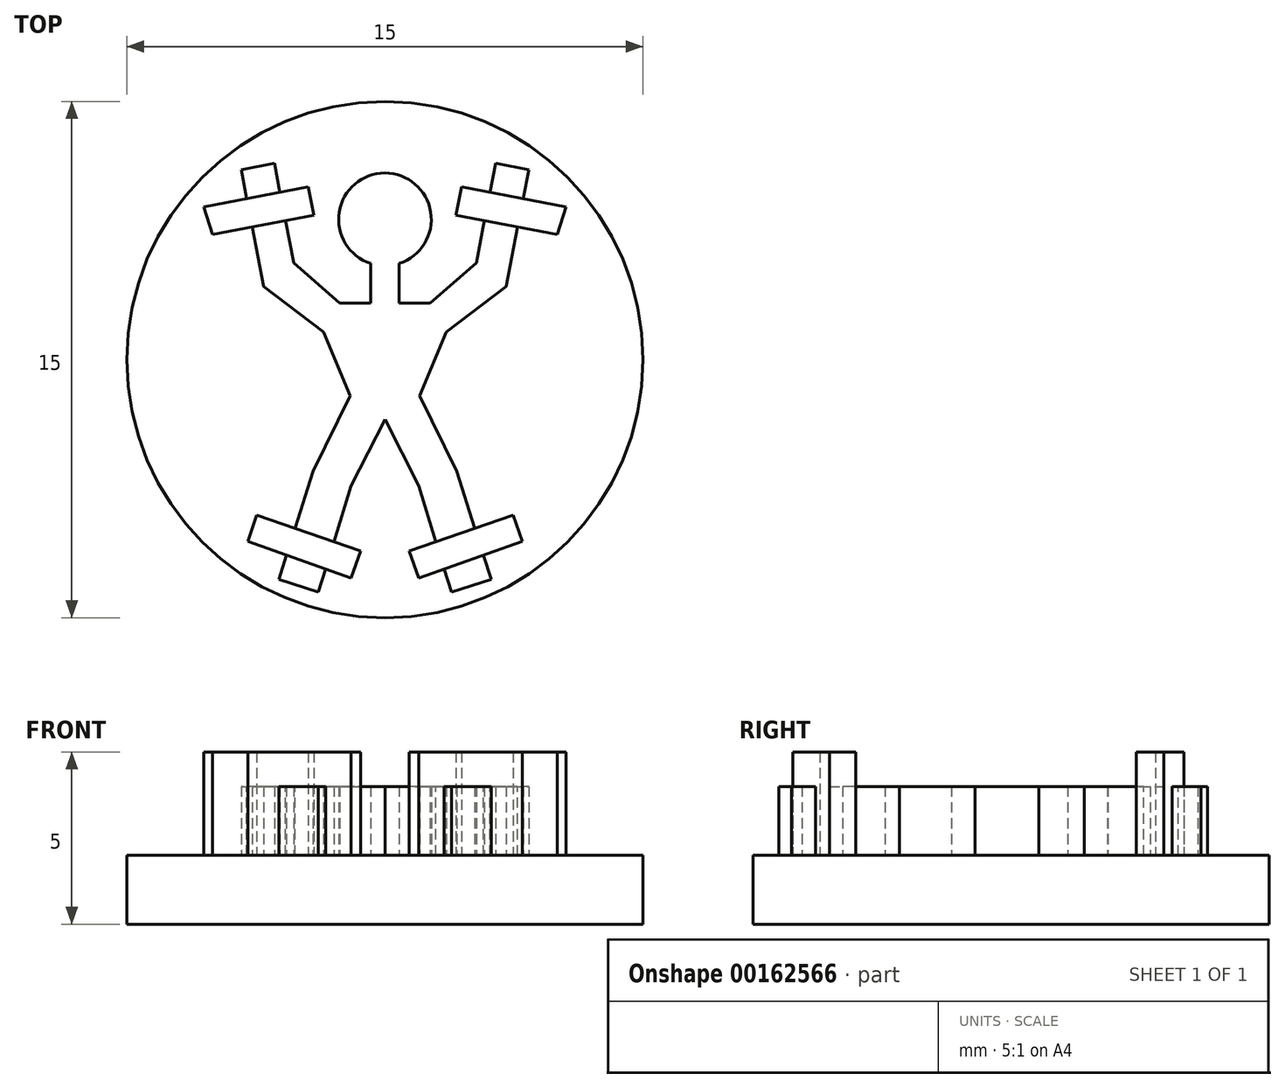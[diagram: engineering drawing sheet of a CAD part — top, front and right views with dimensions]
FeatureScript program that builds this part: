
annotation { "Feature Type Name" : "Feature", "Feature Type Description" : "" }
export const myFeature = defineFeature(function(context is Context, id is Id, definition is map)
    precondition{}
    {
        {
            var Q0;
            Q0=qCreatedBy(makeId("Top.planeOp"),FACE);
            var sketch = newSketch(context, id + "F0", { "sketchPlane" : qUnion([Q0])});
            skCircle(sketch, "E0", {"center": v(0, 0) * mm, "radius": 7.5 * mm});
            skSolve(sketch);
        }
        {
            var Q0;
            Q0 = qSketchRegion(id + "F0", true);
            extrude(context, id + "F1", {"entities" : qUnion([Q0]), "depth" : 2 * mm});
        }
        {
            var Q0;
            Q0=makeQuery(id+"F1.opExtrude","CAP_FACE",FACE,{"disambiguationData":[OSD([sQuery(id+"F0.wireOp",EDGE,"E0")])],"isStart":false});
            var sketch = newSketch(context, id + "F2", { "sketchPlane" : qUnion([Q0])});
            skArc(sketch, "E1", {"start": v(0, 5.42) * mm, "mid": v(-1.33, 4.29) * mm, "end": v(-0.42, 2.8) * mm});
            skLineSegment(sketch, "E2", {"start": v(-0.42, 2.8) * mm, "end": v(-0.42, 1.64) * mm});
            skLineSegment(sketch, "E3", {"start": v(-0.42, 1.64) * mm, "end": v(-1.32, 1.64) * mm});
            skLineSegment(sketch, "E4", {"start": v(-1.32, 1.64) * mm, "end": v(-2.65, 2.8) * mm});
            skLineSegment(sketch, "E5", {"start": v(-2.65, 2.8) * mm, "end": v(-3.21, 5.7) * mm});
            skLineSegment(sketch, "E6", {"start": v(-3.21, 5.7) * mm, "end": v(-4.18, 5.52) * mm});
            skLineSegment(sketch, "E7", {"start": v(-4.18, 5.52) * mm, "end": v(-3.52, 2.12) * mm});
            skLineSegment(sketch, "E8", {"start": v(-3.52, 2.12) * mm, "end": v(-1.79, 0.8) * mm});
            skLineSegment(sketch, "E9", {"start": v(-1.79, 0.8) * mm, "end": v(-1.01, -1.05) * mm});
            skLineSegment(sketch, "E10", {"start": v(-1.01, -1.05) * mm, "end": v(-2.09, -3.24) * mm});
            skLineSegment(sketch, "E11", {"start": v(-2.09, -3.24) * mm, "end": v(-3.08, -6.39) * mm});
            skLineSegment(sketch, "E12", {"start": v(-3.08, -6.39) * mm, "end": v(-1.93, -6.75) * mm});
            skLineSegment(sketch, "E13", {"start": v(-1.93, -6.75) * mm, "end": v(-0.98, -3.67) * mm});
            skLineSegment(sketch, "E14", {"start": v(-0.98, -3.67) * mm, "end": v(0, -1.74) * mm});
            skLineSegment(sketch, "E15", {"start": v(0, -1.74) * mm, "end": v(0, 5.42) * mm});
            skLineSegment(sketch, "E16", {"start": v(0, 9.15) * mm, "end": v(0, -8.52) * mm, "construction": true});
            skArc(sketch, "E17.MirrorCS", {"start": v(0, 5.42) * mm, "mid": v(1.33, 4.29) * mm, "end": v(0.42, 2.8) * mm});
            skLineSegment(sketch, "E18.MirrorCS", {"start": v(0.42, 2.8) * mm, "end": v(0.42, 1.64) * mm});
            skLineSegment(sketch, "E19.MirrorCS", {"start": v(0.42, 1.64) * mm, "end": v(1.32, 1.64) * mm});
            skLineSegment(sketch, "E20.MirrorCS", {"start": v(1.32, 1.64) * mm, "end": v(2.65, 2.8) * mm});
            skLineSegment(sketch, "E21.MirrorCS", {"start": v(2.65, 2.8) * mm, "end": v(3.21, 5.7) * mm});
            skLineSegment(sketch, "E22.MirrorCS", {"start": v(3.21, 5.7) * mm, "end": v(4.18, 5.52) * mm});
            skLineSegment(sketch, "E23.MirrorCS", {"start": v(4.18, 5.52) * mm, "end": v(3.52, 2.12) * mm});
            skLineSegment(sketch, "E24.MirrorCS", {"start": v(3.52, 2.12) * mm, "end": v(1.79, 0.8) * mm});
            skLineSegment(sketch, "E25.MirrorCS", {"start": v(1.79, 0.8) * mm, "end": v(1.01, -1.05) * mm});
            skLineSegment(sketch, "E26.MirrorCS", {"start": v(1.01, -1.05) * mm, "end": v(2.09, -3.24) * mm});
            skLineSegment(sketch, "E27.MirrorCS", {"start": v(2.09, -3.24) * mm, "end": v(3.08, -6.39) * mm});
            skLineSegment(sketch, "E28.MirrorCS", {"start": v(3.08, -6.39) * mm, "end": v(1.93, -6.75) * mm});
            skLineSegment(sketch, "E29.MirrorCS", {"start": v(1.93, -6.75) * mm, "end": v(0.98, -3.67) * mm});
            skLineSegment(sketch, "E30.MirrorCS", {"start": v(0.98, -3.67) * mm, "end": v(0, -1.74) * mm});
            skSolve(sketch);
        }
        {
            var Q0;
            Q0 = qSketchRegion(id + "F2", true);
            extrude(context, id + "F3", {"entities" : qUnion([Q0]), "operationType" : NewBodyOperationType.ADD, "depth" : 2 * mm});
        }
        {
            var Q0;
            Q0=makeQuery(id+"F1.opExtrude","CAP_FACE",FACE,{"disambiguationData":[OSD([sQuery(id+"F0.wireOp",EDGE,"E0")])],"isStart":false});
            var sketch = newSketch(context, id + "F4", { "sketchPlane" : qUnion([Q0])});
            skLineSegment(sketch, "E31", {"start": v(0, 8.76) * mm, "end": v(0, -8.68) * mm, "construction": true});
            skLineSegment(sketch, "E32", {"start": v(-5.26, 4.43) * mm, "end": v(-2.23, 5.02) * mm});
            skLineSegment(sketch, "E33", {"start": v(-2.23, 5.02) * mm, "end": v(-2.07, 4.2) * mm});
            skLineSegment(sketch, "E34", {"start": v(-2.07, 4.2) * mm, "end": v(-5.01, 3.63) * mm});
            skLineSegment(sketch, "E35", {"start": v(-5.01, 3.63) * mm, "end": v(-5.26, 4.43) * mm});
            skLineSegment(sketch, "E36", {"start": v(-3.73, -4.51) * mm, "end": v(-0.7, -5.55) * mm});
            skLineSegment(sketch, "E37", {"start": v(-0.7, -5.55) * mm, "end": v(-0.98, -6.34) * mm});
            skLineSegment(sketch, "E38", {"start": v(-0.98, -6.34) * mm, "end": v(-3.99, -5.28) * mm});
            skLineSegment(sketch, "E39", {"start": v(-3.99, -5.28) * mm, "end": v(-3.73, -4.51) * mm});
            skLineSegment(sketch, "E40.MirrorCS", {"start": v(5.26, 4.43) * mm, "end": v(2.23, 5.02) * mm});
            skLineSegment(sketch, "E41.MirrorCS", {"start": v(2.07, 4.2) * mm, "end": v(5.01, 3.63) * mm});
            skLineSegment(sketch, "E42.MirrorCS", {"start": v(2.23, 5.02) * mm, "end": v(2.07, 4.2) * mm});
            skLineSegment(sketch, "E43.MirrorCS", {"start": v(5.01, 3.63) * mm, "end": v(5.26, 4.43) * mm});
            skLineSegment(sketch, "E44.MirrorCS", {"start": v(3.73, -4.51) * mm, "end": v(0.7, -5.55) * mm});
            skLineSegment(sketch, "E45.MirrorCS", {"start": v(0.98, -6.34) * mm, "end": v(3.99, -5.28) * mm});
            skLineSegment(sketch, "E46.MirrorCS", {"start": v(0.7, -5.55) * mm, "end": v(0.98, -6.34) * mm});
            skLineSegment(sketch, "E47.MirrorCS", {"start": v(3.99, -5.28) * mm, "end": v(3.73, -4.51) * mm});
            skSolve(sketch);
        }
        {
            var Q0;
            Q0 = qSketchRegion(id + "F4", true);
            extrude(context, id + "F5", {"entities" : qUnion([Q0]), "operationType" : NewBodyOperationType.ADD, "depth" : 3 * mm});
        }
    });
